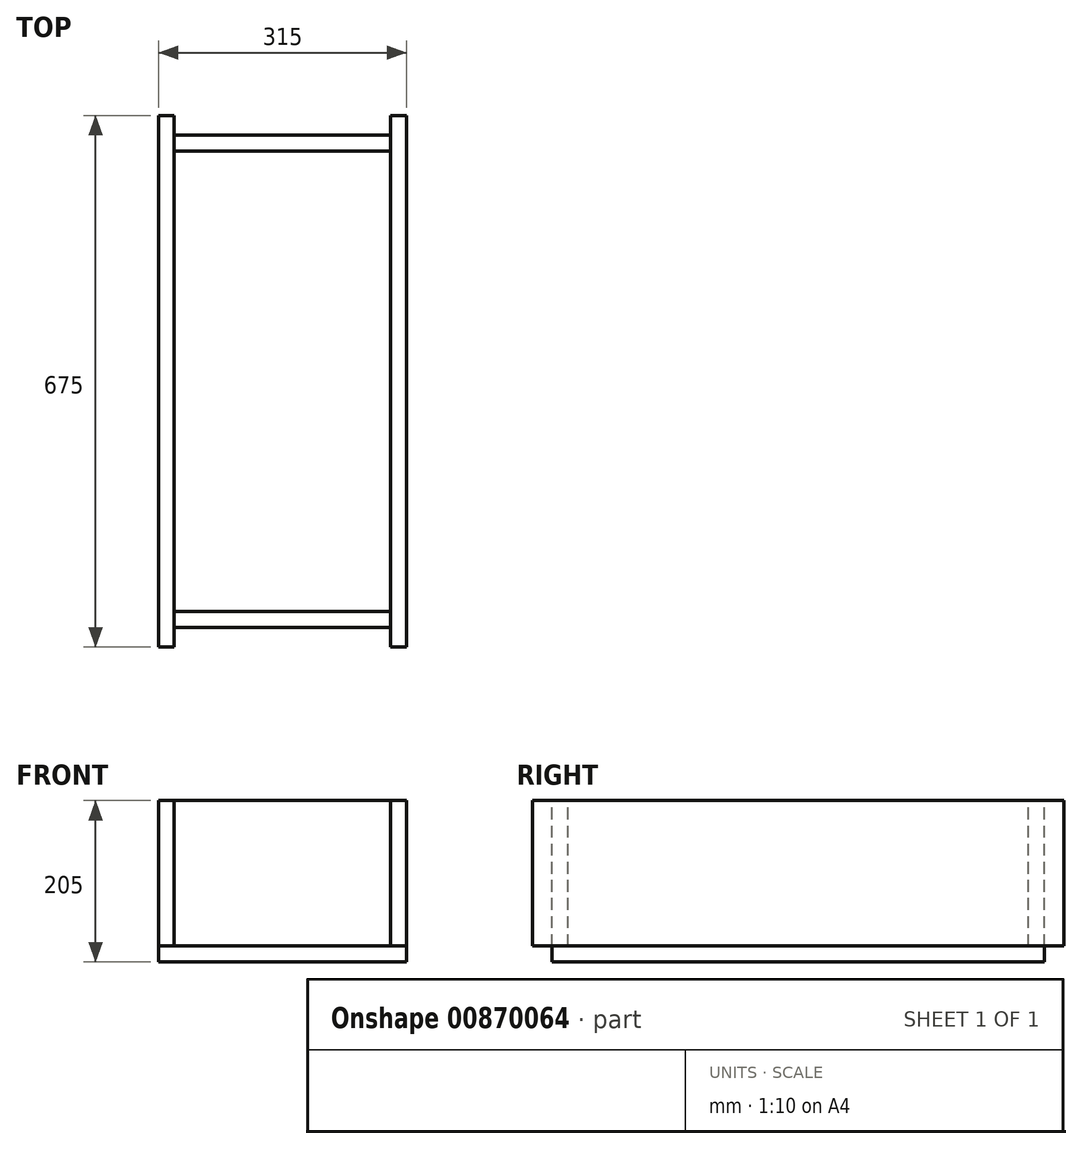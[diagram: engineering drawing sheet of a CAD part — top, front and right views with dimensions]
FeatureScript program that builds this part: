
annotation { "Feature Type Name" : "Feature", "Feature Type Description" : "" }
export const myFeature = defineFeature(function(context is Context, id is Id, definition is map)
    precondition{}
    {
        {
            var Q0;
            Q0=qCreatedBy(makeId("Top.planeOp"),FACE);
            var sketch = newSketch(context, id + "F0", { "sketchPlane" : qUnion([Q0])});
            skLineSegment(sketch, "E0.bottom", {"start": v(157.5, 312.5) * mm, "end": v(-157.5, 312.5) * mm});
            skLineSegment(sketch, "E0.top", {"start": v(157.5, -312.5) * mm, "end": v(-157.5, -312.5) * mm});
            skLineSegment(sketch, "E0.left", {"start": v(157.5, 312.5) * mm, "end": v(157.5, -312.5) * mm});
            skLineSegment(sketch, "E0.right", {"start": v(-157.5, 312.5) * mm, "end": v(-157.5, -312.5) * mm});
            skPoint(sketch, "E0.middle", {"position": v(0, 0) * mm});
            skSolve(sketch);
        }
        {
            var Q0;
            Q0 = qSketchRegion(id + "F0", true);
            extrude(context, id + "F1", {"entities" : qUnion([Q0]), "depth" : 20 * mm, "offsetDistance" : 25 * mm});
        }
        {
            var Q0;
            Q0=makeQuery(id+"F1.opExtrude","SWEPT_FACE",FACE,{"disambiguationData":[OSD([sQuery(id+"F0.wireOp",EDGE,"E0.left")])]});
            var sketch = newSketch(context, id + "F2", { "sketchPlane" : qUnion([Q0])});
            skLineSegment(sketch, "E1.bottom", {"start": v(-337.5, 20) * mm, "end": v(337.5, 20) * mm});
            skLineSegment(sketch, "E1.top", {"start": v(-337.5, 205) * mm, "end": v(337.5, 205) * mm});
            skLineSegment(sketch, "E1.left", {"start": v(-337.5, 20) * mm, "end": v(-337.5, 205) * mm});
            skLineSegment(sketch, "E1.right", {"start": v(337.5, 20) * mm, "end": v(337.5, 205) * mm});
            skPoint(sketch, "E2", {"position": v(0, 20) * mm});
            skSolve(sketch);
        }
        {
            var Q0;
            Q0 = qSketchRegion(id + "F2", true);
            extrude(context, id + "F3", {"entities" : qUnion([Q0]), "oppositeDirection" : true, "depth" : 20 * mm, "offsetDistance" : 25 * mm});
        }
        {
            var Q0;
            Q0=makeQuery(id+"F1.opExtrude","SWEPT_FACE",FACE,{"disambiguationData":[OSD([sQuery(id+"F0.wireOp",EDGE,"E0.right")])]});
            var sketch = newSketch(context, id + "F4", { "sketchPlane" : qUnion([Q0])});
            skLineSegment(sketch, "E3.bottom", {"start": v(-337.5, 20) * mm, "end": v(337.5, 20) * mm});
            skLineSegment(sketch, "E3.top", {"start": v(-337.5, 205) * mm, "end": v(337.5, 205) * mm});
            skLineSegment(sketch, "E3.left", {"start": v(-337.5, 20) * mm, "end": v(-337.5, 205) * mm});
            skLineSegment(sketch, "E3.right", {"start": v(337.5, 20) * mm, "end": v(337.5, 205) * mm});
            skPoint(sketch, "E4", {"position": v(0, 20) * mm});
            skSolve(sketch);
        }
        {
            var Q0;
            Q0 = qSketchRegion(id + "F4", true);
            extrude(context, id + "F5", {"entities" : qUnion([Q0]), "oppositeDirection" : true, "depth" : 20 * mm, "offsetDistance" : 25 * mm});
        }
        {
            var Q0;
            Q0=makeQuery(id+"F1.opExtrude","SWEPT_FACE",FACE,{"disambiguationData":[OSD([sQuery(id+"F0.wireOp",EDGE,"E0.bottom")])]});
            var sketch = newSketch(context, id + "F6", { "sketchPlane" : qUnion([Q0])});
            skLineSegment(sketch, "E5.bottom", {"start": v(-137.5, 20) * mm, "end": v(137.5, 20) * mm});
            skLineSegment(sketch, "E5.top", {"start": v(-137.5, 205) * mm, "end": v(137.5, 205) * mm});
            skLineSegment(sketch, "E5.left", {"start": v(-137.5, 20) * mm, "end": v(-137.5, 205) * mm});
            skLineSegment(sketch, "E5.right", {"start": v(137.5, 20) * mm, "end": v(137.5, 205) * mm});
            skSolve(sketch);
        }
        {
            var Q0;
            Q0=makeQuery(id+"F6.imprint","IMPRINT",FACE,{"disambiguationData":[TD([[makeQuery(id+"F6.imprint","IMPRINT",EDGE,{"derivedFrom":sQuery(id+"F6.wireOp",EDGE,"E5.bottom")}),1.0]])]});
            extrude(context, id + "F7", {"entities" : qUnion([Q0]), "oppositeDirection" : true, "depth" : 20 * mm, "offsetDistance" : 25 * mm});
        }
        {
            var Q0;
            Q0=makeQuery(id+"F1.opExtrude","SWEPT_FACE",FACE,{"disambiguationData":[OSD([sQuery(id+"F0.wireOp",EDGE,"E0.top")])]});
            var sketch = newSketch(context, id + "F8", { "sketchPlane" : qUnion([Q0])});
            skLineSegment(sketch, "E6.bottom", {"start": v(-137.5, 20) * mm, "end": v(137.5, 20) * mm});
            skLineSegment(sketch, "E6.top", {"start": v(-137.5, 205) * mm, "end": v(137.5, 205) * mm});
            skLineSegment(sketch, "E6.left", {"start": v(-137.5, 20) * mm, "end": v(-137.5, 205) * mm});
            skLineSegment(sketch, "E6.right", {"start": v(137.5, 20) * mm, "end": v(137.5, 205) * mm});
            skSolve(sketch);
        }
        {
            var Q0;
            Q0=makeQuery(id+"F8.imprint","IMPRINT",FACE,{"disambiguationData":[TD([[makeQuery(id+"F8.imprint","IMPRINT",EDGE,{"derivedFrom":sQuery(id+"F8.wireOp",EDGE,"E6.bottom")}),-1.0]])]});
            extrude(context, id + "F9", {"entities" : qUnion([Q0]), "oppositeDirection" : true, "depth" : 20 * mm, "offsetDistance" : 25 * mm});
        }
    });
